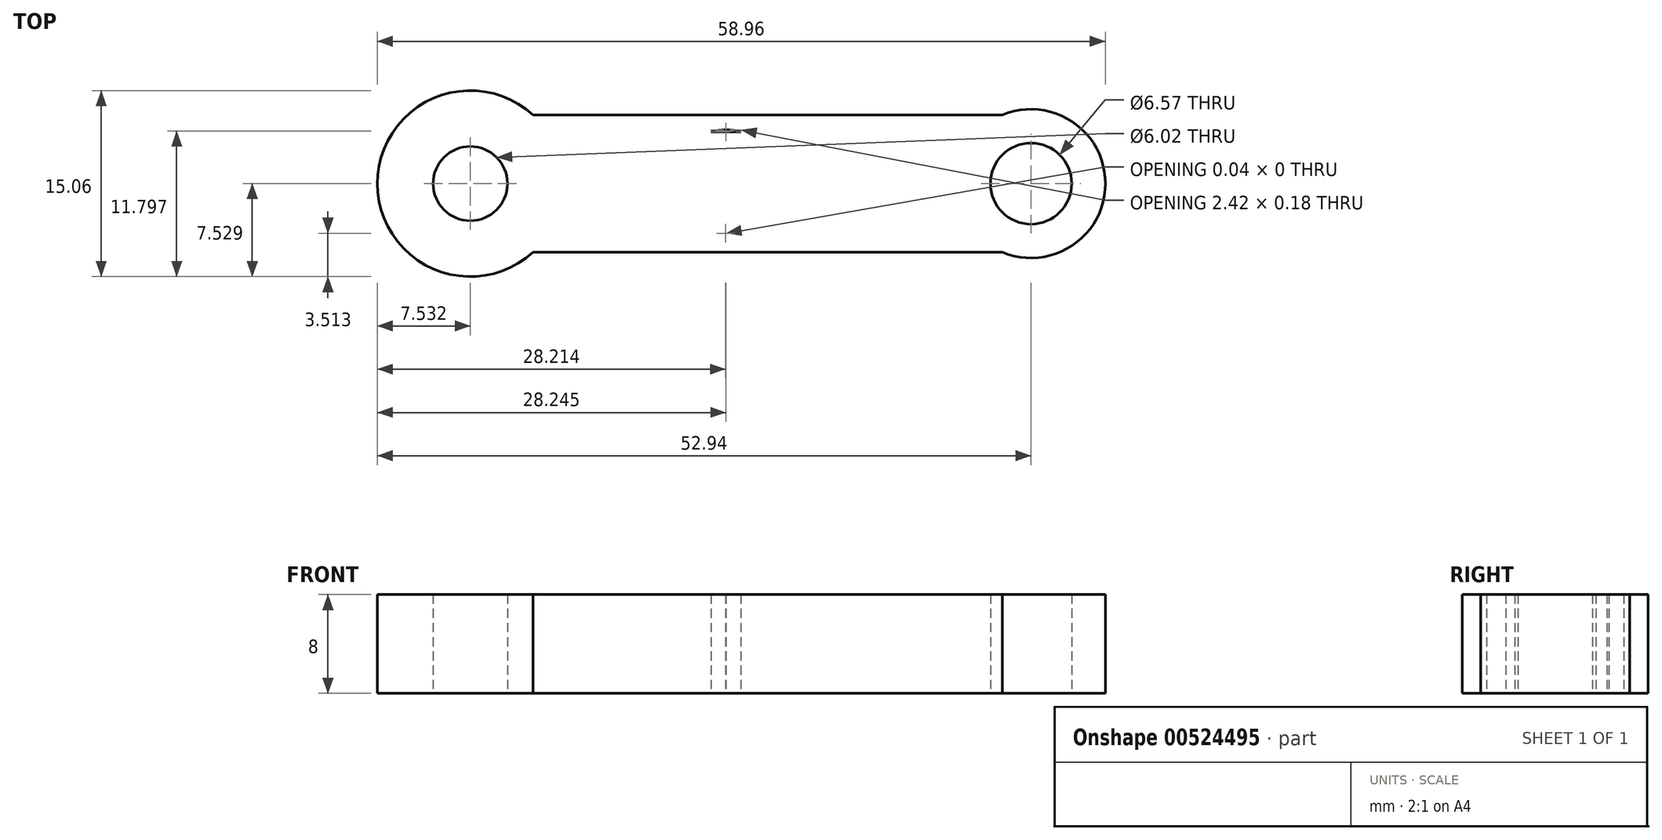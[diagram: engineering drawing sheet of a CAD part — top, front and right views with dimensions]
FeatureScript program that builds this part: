
annotation { "Feature Type Name" : "Feature", "Feature Type Description" : "" }
export const myFeature = defineFeature(function(context is Context, id is Id, definition is map)
    precondition{}
    {
        {
            var Q0;
            Q0=qCreatedBy(makeId("Top.planeOp"),FACE);
            var sketch = newSketch(context, id + "F0", { "sketchPlane" : qUnion([Q0])});
            skLineSegment(sketch, "E0", {"start": v(-40.33, 23.5) * mm, "end": v(-40.33, 12.38) * mm});
            skLineSegment(sketch, "E1", {"start": v(-40.33, 12.38) * mm, "end": v(-2.33, 12.38) * mm});
            skLineSegment(sketch, "E2", {"start": v(-2.33, 12.38) * mm, "end": v(-2.33, 23.5) * mm});
            skLineSegment(sketch, "E3", {"start": v(-2.33, 23.5) * mm, "end": v(-40.33, 23.5) * mm});
            skCircle(sketch, "E4", {"center": v(-45.4, 17.94) * mm, "radius": 7.53 * mm});
            skPoint(sketch, "E4.centerSnap0", {"position": v(-40.33, 17.94) * mm});
            skCircle(sketch, "E5", {"center": v(0, 17.94) * mm, "radius": 6.02 * mm});
            skCircle(sketch, "E6", {"center": v(-45.4, 17.94) * mm, "radius": 3.01 * mm});
            skCircle(sketch, "E7", {"center": v(0, 17.94) * mm, "radius": 3.29 * mm});
            skCircle(sketch, "E8", {"center": v(-45.4, 17.94) * mm, "radius": 4.55 * mm});
            skLineSegment(sketch, "E9", {"start": v(-43.6, 22.12) * mm, "end": v(-25.9, 22.12) * mm});
            skLineSegment(sketch, "E10", {"start": v(-43.6, 13.76) * mm, "end": v(-25.9, 13.76) * mm});
            skArc(sketch, "E11", {"start": v(-25.9, 13.76) * mm, "mid": v(-21.72, 17.94) * mm, "end": v(-25.9, 22.12) * mm});
            skArc(sketch, "E12", {"start": v(-24.75, 13.92) * mm, "mid": v(-20.55, 18.7) * mm, "end": v(-25.9, 22.12) * mm});
            skLineSegment(sketch, "E13", {"start": v(-25.9, 22.12) * mm, "end": v(-7.88, 22.12) * mm});
            skLineSegment(sketch, "E14", {"start": v(-7.88, 22.12) * mm, "end": v(-7.88, 13.8) * mm});
            skLineSegment(sketch, "E15", {"start": v(-7.88, 13.8) * mm, "end": v(-24.75, 13.92) * mm});
            skSolve(sketch);
        }
        {
            var Q0;
            {var subQ1=sQuery(id+"F0.wireOp",EDGE,"E2");var subQ3=sQuery(id+"F0.wireOp",EDGE,"E7");var subQ4=makeQuery(id+"F0.imprint","INTERSECT",VERTEX,{"disambiguationData":[OD(0.0)],"derivedFrom":[subQ1,subQ3]});Q0=makeQuery(id+"F0.imprint","IMPRINT",FACE,{"disambiguationData":[TD([[makeQuery(id+"F0.imprint","IMPRINT",EDGE,{"disambiguationData":[TD([[subQ4,-1.0]])],"derivedFrom":subQ3}),-1.0]])]});}
            var Q1;
            {var subQ1=sQuery(id+"F0.wireOp",EDGE,"E0");var subQ3=sQuery(id+"F0.wireOp",EDGE,"E9");var subQ4=makeQuery(id+"F0.imprint","INTERSECT",VERTEX,{"derivedFrom":[subQ1,subQ3]});Q1=makeQuery(id+"F0.imprint","IMPRINT",FACE,{"disambiguationData":[TD([[makeQuery(id+"F0.imprint","IMPRINT",EDGE,{"disambiguationData":[TD([[subQ4,-1.0]])],"derivedFrom":subQ3}),1.0]])]});}
            var Q2;
            {var subQ1=sQuery(id+"F0.wireOp",EDGE,"E0");var subQ3=sQuery(id+"F0.wireOp",EDGE,"E10");var subQ4=makeQuery(id+"F0.imprint","INTERSECT",VERTEX,{"derivedFrom":[subQ1,subQ3]});Q2=makeQuery(id+"F0.imprint","IMPRINT",FACE,{"disambiguationData":[TD([[makeQuery(id+"F0.imprint","IMPRINT",EDGE,{"disambiguationData":[TD([[subQ4,-1.0]])],"derivedFrom":subQ3}),-1.0]])]});}
            var Q3;
            {var subQ1=sQuery(id+"F0.wireOp",EDGE,"E2");var subQ3=sQuery(id+"F0.wireOp",EDGE,"E7");var subQ4=makeQuery(id+"F0.imprint","INTERSECT",VERTEX,{"disambiguationData":[OD(0.0)],"derivedFrom":[subQ1,subQ3]});Q3=makeQuery(id+"F0.imprint","IMPRINT",FACE,{"disambiguationData":[TD([[makeQuery(id+"F0.imprint","IMPRINT",EDGE,{"disambiguationData":[TD([[subQ4,1.0]])],"derivedFrom":subQ3}),-1.0]])]});}
            var Q4;
            {var subQ4=sQuery(id+"F0.wireOp",EDGE,"E9");var subQ5=sQuery(id+"F0.wireOp",EDGE,"E8");var subQ6=makeQuery(id+"F0.imprint","INTERSECT",VERTEX,{"derivedFrom":[subQ5,subQ4]});Q4=makeQuery(id+"F0.imprint","IMPRINT",FACE,{"disambiguationData":[TD([[makeQuery(id+"F0.imprint","IMPRINT",EDGE,{"disambiguationData":[TD([[subQ6,-1.0]])],"derivedFrom":subQ5}),-1.0]])]});}
            var Q5;
            {var subQ4=sQuery(id+"F0.wireOp",EDGE,"E4");var subQ6=sQuery(id+"F0.wireOp",EDGE,"E9");var subQ8=makeQuery(id+"F0.imprint","INTERSECT",VERTEX,{"derivedFrom":[subQ4,subQ6]});Q5=makeQuery(id+"F0.imprint","IMPRINT",FACE,{"disambiguationData":[TD([[makeQuery(id+"F0.imprint","IMPRINT",EDGE,{"disambiguationData":[TD([[subQ8,1.0]])],"derivedFrom":subQ4}),-1.0]])]});}
            var Q6;
            {var subQ5=sQuery(id+"F0.wireOp",EDGE,"E14");Q6=makeQuery(id+"F0.imprint","IMPRINT",FACE,{"disambiguationData":[TD([[makeQuery(id+"F0.imprint","IMPRINT",EDGE,{"derivedFrom":subQ5}),-1.0]])]});}
            var Q7;
            {var subQ1=sQuery(id+"F0.wireOp",EDGE,"E12");var subQ4=sQuery(id+"F0.wireOp",EDGE,"E15");var subQ6=makeQuery(id+"F0.imprint","INTERSECT",VERTEX,{"derivedFrom":[subQ1,subQ4]});Q7=makeQuery(id+"F0.imprint","IMPRINT",FACE,{"disambiguationData":[TD([[makeQuery(id+"F0.imprint","IMPRINT",EDGE,{"disambiguationData":[TD([[subQ6,-1.0]])],"derivedFrom":subQ1}),1.0]])]});}
            var Q8;
            {var subQ12=sQuery(id+"F0.wireOp",EDGE,"E1");Q8=makeQuery(id+"F0.imprint","IMPRINT",FACE,{"disambiguationData":[TD([[makeQuery(id+"F0.imprint","IMPRINT",EDGE,{"derivedFrom":subQ12}),1.0]])]});}
            var Q9;
            {var subQ0=sQuery(id+"F0.wireOp",EDGE,"E9");var subQ1=sQuery(id+"F0.wireOp",EDGE,"E0");var subQ2=makeQuery(id+"F0.imprint","INTERSECT",VERTEX,{"derivedFrom":[subQ1,subQ0]});Q9=makeQuery(id+"F0.imprint","IMPRINT",FACE,{"disambiguationData":[TD([[makeQuery(id+"F0.imprint","IMPRINT",EDGE,{"disambiguationData":[TD([[subQ2,-1.0]])],"derivedFrom":subQ1}),1.0]])]});}
            var Q10;
            {var subQ0=sQuery(id+"F0.wireOp",EDGE,"E9");var subQ1=sQuery(id+"F0.wireOp",EDGE,"E0");var subQ2=makeQuery(id+"F0.imprint","INTERSECT",VERTEX,{"derivedFrom":[subQ1,subQ0]});Q10=makeQuery(id+"F0.imprint","IMPRINT",FACE,{"disambiguationData":[TD([[makeQuery(id+"F0.imprint","IMPRINT",EDGE,{"disambiguationData":[TD([[subQ2,-1.0]])],"derivedFrom":subQ1}),-1.0]])]});}
            var Q11;
            Q11=makeQuery(id+"F0.imprint","IMPRINT",FACE,{"disambiguationData":[TD([[makeQuery(id+"F0.imprint","IMPRINT",EDGE,{"derivedFrom":sQuery(id+"F0.wireOp",EDGE,"E6")}),-1.0]])]});
            extrude(context, id + "F1", {"entities" : qUnion([Q0, Q1, Q2, Q3, Q4, Q5, Q6, Q7, Q8, Q9, Q10, Q11]), "depth" : 8 * mm, "offsetDistance" : 25 * mm});
        }
    });
